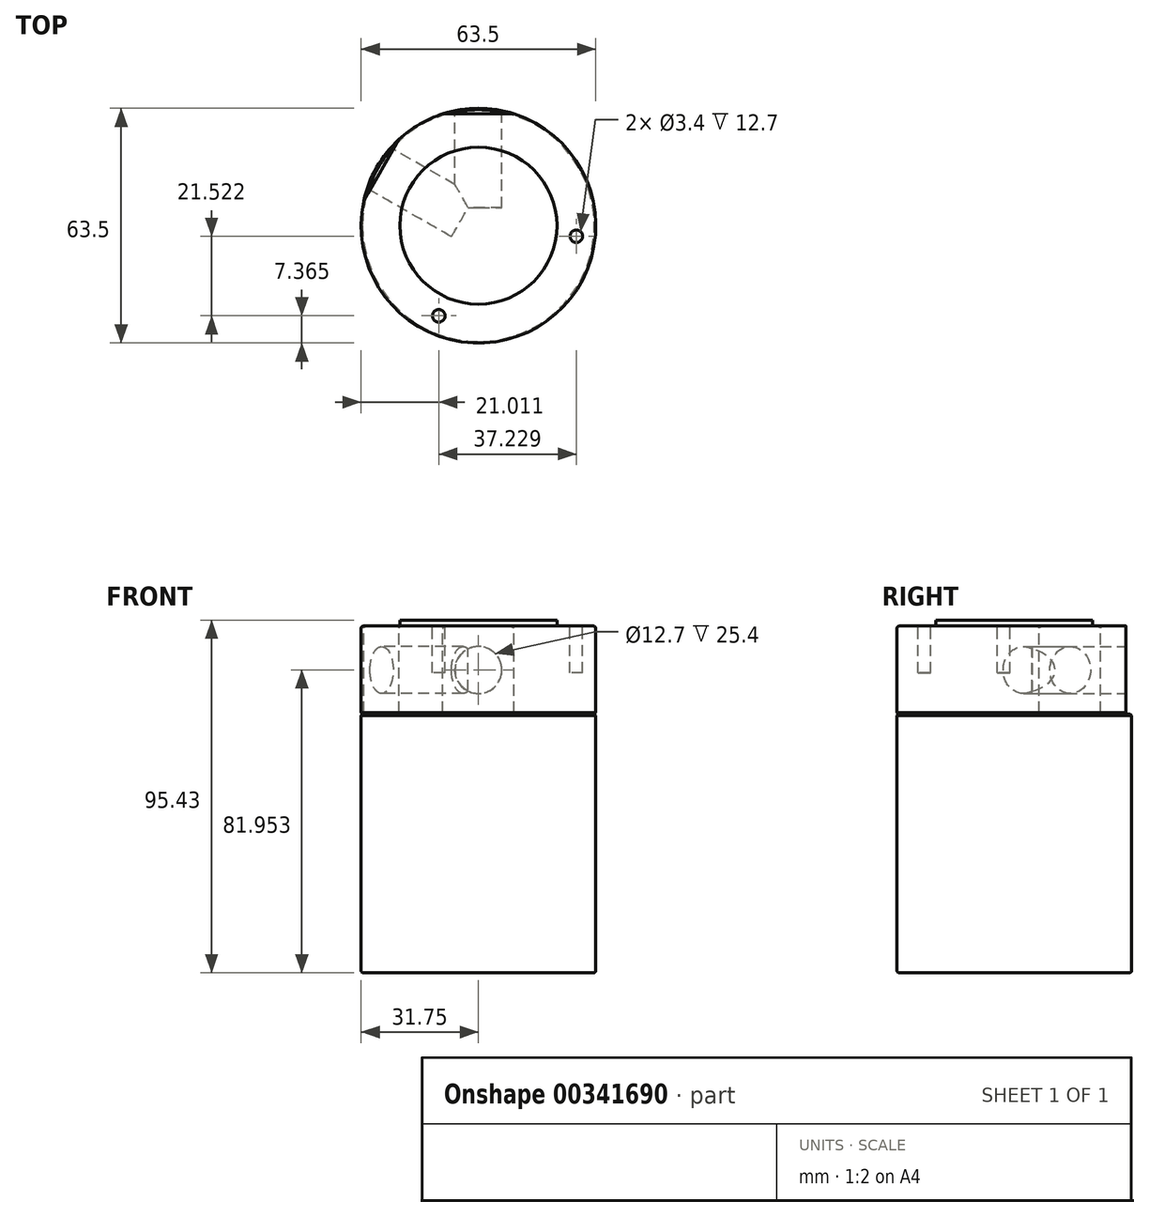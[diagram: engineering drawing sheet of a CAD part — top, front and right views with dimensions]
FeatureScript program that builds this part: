
annotation { "Feature Type Name" : "Feature", "Feature Type Description" : "" }
export const myFeature = defineFeature(function(context is Context, id is Id, definition is map)
    precondition{}
    {
        {
            var Q0;
            Q0=qCreatedBy(makeId("Top.planeOp"),FACE);
            var sketch = newSketch(context, id + "F0", { "sketchPlane" : qUnion([Q0])});
            skCircle(sketch, "E0", {"center": v(0, 0) * mm, "radius": 31.75 * mm});
            skSolve(sketch);
        }
        {
            var Q0;
            Q0=makeQuery(id+"F0.imprint","IMPRINT",FACE,{"disambiguationData":[TD([[makeQuery(id+"F0.imprint","IMPRINT",EDGE,{"derivedFrom":sQuery(id+"F0.wireOp",EDGE,"E0")}),1.0]])]});
            extrude(context, id + "F1", {"entities" : qUnion([Q0]), "depth" : 93.85 * mm});
        }
        {
            var Q0;
            Q0=makeQuery(id+"F1.opExtrude","CAP_FACE",FACE,{"disambiguationData":[OSD([sQuery(id+"F0.wireOp",EDGE,"E0")])],"isStart":false});
            var sketch = newSketch(context, id + "F2", { "sketchPlane" : qUnion([Q0])});
            skCircle(sketch, "E1", {"center": v(0, 0) * mm, "radius": 21.25 * mm});
            skSolve(sketch);
        }
        {
            var Q0;
            Q0=makeQuery(id+"F2.imprint","IMPRINT",FACE,{"disambiguationData":[TD([[makeQuery(id+"F2.imprint","IMPRINT",EDGE,{"derivedFrom":sQuery(id+"F2.wireOp",EDGE,"E1")}),1.0]])]});
            extrude(context, id + "F3", {"entities" : qUnion([Q0]), "operationType" : NewBodyOperationType.ADD, "depth" : 1.57 * mm});
        }
        {
            var Q0;
            Q0=makeQuery(id+"F1.opExtrude","CAP_FACE",FACE,{"disambiguationData":[OSD([sQuery(id+"F0.wireOp",EDGE,"E0")])],"isStart":false});
            var sketch = newSketch(context, id + "F4", { "sketchPlane" : qUnion([Q0])});
            skArc(sketch, "E2", {"start": v(9.64, 30.25) * mm, "mid": v(0, 31.75) * mm, "end": v(-9.64, 30.25) * mm});
            skLineSegment(sketch, "E3", {"start": v(-9.64, 30.25) * mm, "end": v(9.64, 30.25) * mm});
            skSolve(sketch);
        }
        {
            var Q0;
            Q0=makeQuery(id+"F4.imprint","IMPRINT",FACE,{"disambiguationData":[TD([[makeQuery(id+"F4.imprint","IMPRINT",EDGE,{"derivedFrom":sQuery(id+"F4.wireOp",EDGE,"E2")}),1.0]])]});
            extrude(context, id + "F5", {"entities" : qUnion([Q0]), "operationType" : NewBodyOperationType.REMOVE, "oppositeDirection" : true, "depth" : 23.8 * mm});
        }
        {
            var Q0;
            Q0=makeQuery(id+"F1.opExtrude","CAP_FACE",FACE,{"disambiguationData":[OSD([sQuery(id+"F0.wireOp",EDGE,"E0")])],"isStart":false});
            var sketch = newSketch(context, id + "F6", { "sketchPlane" : qUnion([Q0])});
            skArc(sketch, "E4", {"start": v(-21.46, 23.4) * mm, "mid": v(-27.55, 15.78) * mm, "end": v(-31.04, 6.67) * mm});
            skLineSegment(sketch, "E5", {"start": v(-21.46, 23.4) * mm, "end": v(-31.04, 6.67) * mm});
            skSolve(sketch);
        }
        {
            var Q0;
            Q0=makeQuery(id+"F6.imprint","IMPRINT",FACE,{"disambiguationData":[TD([[makeQuery(id+"F6.imprint","IMPRINT",EDGE,{"derivedFrom":sQuery(id+"F6.wireOp",EDGE,"E4")}),1.0]])]});
            var Q1;
            Q1=makeQuery(id+"F5.boolean.opBoolean","COPY",FACE,{"derivedFrom":makeQuery(id+"F5.opExtrude","CAP_FACE",FACE,{"disambiguationData":[OSD([sQuery(id+"F4.wireOp",EDGE,"E2"),sQuery(id+"F4.wireOp",EDGE,"E3")])],"isStart":false})});
            extrude(context, id + "F7", {"entities" : qUnion([Q0]), "operationType" : NewBodyOperationType.REMOVE, "endBound" : BoundingType.UP_TO_SURFACE, "oppositeDirection" : true, "endBoundEntityFace" : qUnion([Q1]), "depth" : 25.4 * mm});
        }
        {
            var Q0;
            Q0=makeQuery(id+"F1.opExtrude","CAP_FACE",FACE,{"disambiguationData":[OSD([sQuery(id+"F0.wireOp",EDGE,"E0")])],"isStart":false});
            var sketch = newSketch(context, id + "F8", { "sketchPlane" : qUnion([Q0])});
            skCircle(sketch, "E6", {"center": v(0, 0) * mm, "radius": 26.64 * mm, "construction": true});
            skLineSegment(sketch, "E7", {"start": v(-21.46, 23.4) * mm, "end": v(-9.64, 30.25) * mm, "construction": true});
            skLineSegment(sketch, "E8", {"start": v(-15.55, 26.82) * mm, "end": v(0, 0) * mm, "construction": true});
            skLineSegment(sketch, "E9", {"start": v(0, 0) * mm, "end": v(13.34, -23.07) * mm, "construction": true});
            skCircle(sketch, "E10", {"center": v(26.5, -2.86) * mm, "radius": 1.7 * mm});
            skCircle(sketch, "E11", {"center": v(-10.74, -24.38) * mm, "radius": 1.7 * mm});
            skSolve(sketch);
        }
        {
            var Q0;
            Q0=makeQuery(id+"F8.imprint","IMPRINT",FACE,{"disambiguationData":[TD([[makeQuery(id+"F8.imprint","IMPRINT",EDGE,{"derivedFrom":sQuery(id+"F8.wireOp",EDGE,"E11")}),1.0]])]});
            extrude(context, id + "F9", {"entities" : qUnion([Q0]), "operationType" : NewBodyOperationType.REMOVE, "oppositeDirection" : true, "depth" : 12.7 * mm});
        }
        {
            var Q0;
            Q0=makeQuery(id+"F8.imprint","IMPRINT",FACE,{"disambiguationData":[TD([[makeQuery(id+"F8.imprint","IMPRINT",EDGE,{"derivedFrom":sQuery(id+"F8.wireOp",EDGE,"E10")}),1.0]])]});
            extrude(context, id + "F10", {"entities" : qUnion([Q0]), "operationType" : NewBodyOperationType.REMOVE, "oppositeDirection" : true, "depth" : 12.7 * mm});
        }
        {
            var Q0;
            Q0=makeQuery(id+"F7.boolean.opBoolean","SPLIT",EDGE,{"disambiguationData":[OD(0.0)],"derivedFrom":makeQuery(id+"F1.opExtrude","CAP_EDGE",EDGE,{"disambiguationData":[OSD([sQuery(id+"F0.wireOp",EDGE,"E0")])],"isStart":false})});
            fillet(context, id + "F11", {"entities" : qUnion([Q0]), "radius" : 0.64 * mm, "tangentPropagation" : true, "allowEdgeOverflow" : false});
        }
        {
            var Q0;
            Q0=makeQuery(id+"F7.boolean.opBoolean","SPLIT",EDGE,{"disambiguationData":[OD(1.0)],"derivedFrom":makeQuery(id+"F1.opExtrude","CAP_EDGE",EDGE,{"disambiguationData":[OSD([sQuery(id+"F0.wireOp",EDGE,"E0")])],"isStart":false})});
            fillet(context, id + "F12", {"entities" : qUnion([Q0]), "radius" : 0.64 * mm, "tangentPropagation" : true, "allowEdgeOverflow" : false});
        }
        {
            var Q0;
            Q0=makeQuery(id+"F1.opExtrude","CAP_EDGE",EDGE,{"disambiguationData":[OSD([sQuery(id+"F0.wireOp",EDGE,"E0")])],"isStart":true});
            fillet(context, id + "F13", {"entities" : qUnion([Q0]), "radius" : 0.64 * mm, "tangentPropagation" : true, "allowEdgeOverflow" : false});
        }
        {
            var Q0;
            Q0=makeQuery(id+"F5.boolean.opBoolean","COPY",FACE,{"derivedFrom":makeQuery(id+"F5.opExtrude","SWEPT_FACE",FACE,{"disambiguationData":[OSD([sQuery(id+"F4.wireOp",EDGE,"E3")])]})});
            var sketch = newSketch(context, id + "F14", { "sketchPlane" : qUnion([Q0])});
            skCircle(sketch, "E12", {"center": v(0, 81.95) * mm, "radius": 6.35 * mm});
            skSolve(sketch);
        }
        {
            var Q0;
            Q0=makeQuery(id+"F14.imprint","IMPRINT",FACE,{"disambiguationData":[TD([[makeQuery(id+"F14.imprint","IMPRINT",EDGE,{"derivedFrom":sQuery(id+"F14.wireOp",EDGE,"E12")}),1.0]])]});
            extrude(context, id + "F15", {"entities" : qUnion([Q0]), "operationType" : NewBodyOperationType.REMOVE, "oppositeDirection" : true, "depth" : 25.4 * mm});
        }
        {
            var Q0;
            Q0=makeQuery(id+"F7.boolean.opBoolean","COPY",FACE,{"derivedFrom":makeQuery(id+"F7.opExtrude","SWEPT_FACE",FACE,{"disambiguationData":[OSD([sQuery(id+"F6.wireOp",EDGE,"E5")])]})});
            var sketch = newSketch(context, id + "F16", { "sketchPlane" : qUnion([Q0])});
            skCircle(sketch, "E13", {"center": v(-0.11, 81.95) * mm, "radius": 6.35 * mm});
            skSolve(sketch);
        }
        {
            var Q0;
            Q0=makeQuery(id+"F16.imprint","IMPRINT",FACE,{"disambiguationData":[TD([[makeQuery(id+"F16.imprint","IMPRINT",EDGE,{"derivedFrom":sQuery(id+"F16.wireOp",EDGE,"E13")}),1.0]])]});
            extrude(context, id + "F17", {"entities" : qUnion([Q0]), "operationType" : NewBodyOperationType.REMOVE, "oppositeDirection" : true, "depth" : 25.4 * mm});
        }
        {
            var Q0;
            Q0=makeQuery(id+"F5.boolean.opBoolean","COPY",FACE,{"derivedFrom":makeQuery(id+"F5.opExtrude","CAP_FACE",FACE,{"disambiguationData":[OSD([sQuery(id+"F4.wireOp",EDGE,"E2"),sQuery(id+"F4.wireOp",EDGE,"E3")])],"isStart":false})});
            cPlane(context, id + "F18", {"entities" : qUnion([Q0]), "cplaneType" : CPlaneType.OFFSET, "offset" : 0 * mm, "width" : 152.4 * mm, "height" : 152.4 * mm});
        }
        {
            var Q0;
            Q0=qCreatedBy(makeId("Right.planeOp"),FACE);
            cPlane(context, id + "F19", {"entities" : qUnion([Q0]), "cplaneType" : CPlaneType.OFFSET, "offset" : 31.75 * mm, "width" : 152.4 * mm, "height" : 152.4 * mm});
        }
        {
            var Q0;
            Q0=qCreatedBy(makeId("Front.planeOp"),FACE);
            var sketch = newSketch(context, id + "F20", { "sketchPlane" : qUnion([Q0])});
            skLineSegment(sketch, "E14", {"start": v(31.75, 70.43) * mm, "end": v(31.75, 69.67) * mm});
            skLineSegment(sketch, "E15", {"start": v(31.75, 70.43) * mm, "end": v(31.37, 70.05) * mm});
            skLineSegment(sketch, "E16", {"start": v(31.37, 70.05) * mm, "end": v(31.75, 69.67) * mm});
            skSolve(sketch);
        }
        {
            var Q0;
            Q0=makeQuery(id+"F20.imprint","IMPRINT",FACE,{"disambiguationData":[TD([[makeQuery(id+"F20.imprint","IMPRINT",EDGE,{"derivedFrom":sQuery(id+"F20.wireOp",EDGE,"E14")}),-1.0]])]});
            var Q1;
            Q1=makeQuery(id+"F1.opExtrude","SWEPT_FACE",FACE,{"disambiguationData":[OSD([sQuery(id+"F0.wireOp",EDGE,"E0")])]});
            revolve(context, id + "F21", {"operationType" : NewBodyOperationType.REMOVE, "entities" : qUnion([Q0]), "axis" : qUnion([Q1]), "revolveType" : RevolveType.FULL, "oppositeDirection" : true});
        }
    });
